# Revit family: S1400TAL
name_source: partatom
category: Lighting Fixtures
revit_build: Autodesk Revit 2017 (Build: 20160225_1515(x64)
units: mm (PartAtom-declared; Revit-internal decimal feet)

## family parameters
Cut with Voids When Loaded = No
Host = Face
Light Source = Yes
Part Type = Normal
Room Calculation Point = No
Round Connector Dimension = Use Diameter
Shared = No

## types (1)
- STAL.1400.344.40.90
    Apparent Load = 195 VA
    Color Filter = 16777215
    Default Elevation = 1219 mm
    Description = 344W - 90°
    Dimming Lamp Color Temperature Shift = <None>
    Emit Shape Visible in Rendering = No
    Emit from Rectangle Length = 1431 mm  [stored 4.69488 ft]
    Emit from Rectangle Width = 180 mm  [stored 0.590551 ft]
    Lamp = LED
    Manufacturer = ARLIGHT
    Model = S1400TAL
    Photometric Web File = s1400tal-344w-4k-80ra-vl-105-90oe.ies
    Tilt Angle = -90.00°
    Type Comments = Industrial Lighting
    Type Image = talia-header.jpg
    URL = http://www.arlight.net
    Wattage Comments = 195W

note: [stored X ft] marks values corroborated as IEEE doubles in the binary element streams (Revit-internal decimal feet)

## geometry (parser evidence)
native form markers: Sweep x2
no freeform markers — native parametric forms only
